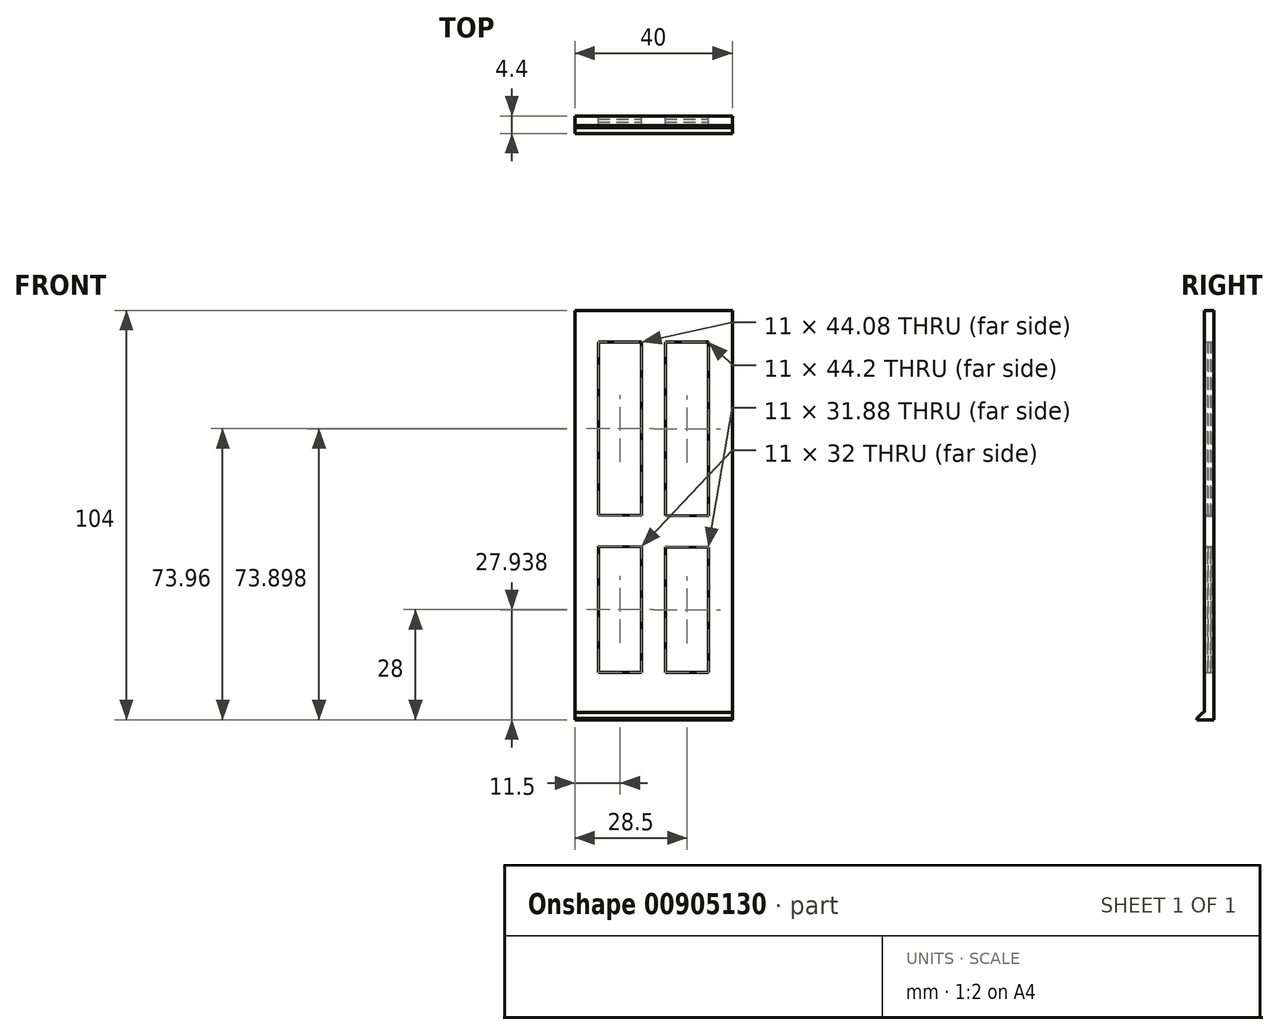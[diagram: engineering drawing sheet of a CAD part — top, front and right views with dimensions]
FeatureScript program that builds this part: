
annotation { "Feature Type Name" : "Feature", "Feature Type Description" : "" }
export const myFeature = defineFeature(function(context is Context, id is Id, definition is map)
    precondition{}
    {
        {
            var Q0;
            Q0=qCreatedBy(makeId("Front.planeOp"),FACE);
            var sketch = newSketch(context, id + "F0", { "sketchPlane" : qUnion([Q0])});
            skLineSegment(sketch, "E0.bottom", {"start": v(20, 52) * mm, "end": v(-20, 52) * mm});
            skLineSegment(sketch, "E0.top", {"start": v(20, -52) * mm, "end": v(-20, -52) * mm});
            skLineSegment(sketch, "E0.left", {"start": v(20, 52) * mm, "end": v(20, -52) * mm});
            skLineSegment(sketch, "E0.right", {"start": v(-20, 52) * mm, "end": v(-20, -52) * mm});
            skPoint(sketch, "E0.middle", {"position": v(0, 0) * mm});
            skLineSegment(sketch, "E1.0", {"start": v(-14, 52) * mm, "end": v(-14, -52) * mm});
            skLineSegment(sketch, "E2.0", {"start": v(14, 52) * mm, "end": v(14, -52.4) * mm});
            skLineSegment(sketch, "E3.0", {"start": v(20, 44) * mm, "end": v(-20, 44) * mm});
            skLineSegment(sketch, "E4.0", {"start": v(20, -40) * mm, "end": v(-20, -40) * mm});
            skLineSegment(sketch, "E5", {"start": v(0, -40) * mm, "end": v(0, 44) * mm, "construction": true});
            skLineSegment(sketch, "E6.0", {"start": v(3, -40) * mm, "end": v(3, 44) * mm});
            skLineSegment(sketch, "E7.0", {"start": v(-3, -40) * mm, "end": v(-3, 44) * mm});
            skLineSegment(sketch, "E8", {"start": v(-14, 0) * mm, "end": v(14, -0.2) * mm, "construction": true});
            skLineSegment(sketch, "E9", {"start": v(-14, 0) * mm, "end": v(14, -0.2) * mm});
            skLineSegment(sketch, "E10.0", {"start": v(-14, -8) * mm, "end": v(14, -8.2) * mm});
            skSolve(sketch);
        }
        {
            var Q0;
            {var subQ0=sQuery(id+"F0.wireOp",EDGE,"E9");var subQ1=sQuery(id+"F0.wireOp",EDGE,"E1.0");var subQ2=makeQuery(id+"F0.imprint","INTERSECT",VERTEX,{"derivedFrom":[subQ1,subQ0]});Q0=makeQuery(id+"F0.imprint","IMPRINT",FACE,{"disambiguationData":[TD([[makeQuery(id+"F0.imprint","IMPRINT",EDGE,{"disambiguationData":[TD([[subQ2,1.0]])],"derivedFrom":subQ1}),1.0]])]});}
            var Q1;
            {var subQ0=sQuery(id+"F0.wireOp",EDGE,"E9");var subQ1=sQuery(id+"F0.wireOp",EDGE,"E2.0");var subQ2=makeQuery(id+"F0.imprint","INTERSECT",VERTEX,{"derivedFrom":[subQ1,subQ0]});Q1=makeQuery(id+"F0.imprint","IMPRINT",FACE,{"disambiguationData":[TD([[makeQuery(id+"F0.imprint","IMPRINT",EDGE,{"disambiguationData":[TD([[subQ2,1.0]])],"derivedFrom":subQ1}),-1.0]])]});}
            var Q2;
            {var subQ0=sQuery(id+"F0.wireOp",EDGE,"E10.0");var subQ1=sQuery(id+"F0.wireOp",EDGE,"E1.0");var subQ2=makeQuery(id+"F0.imprint","INTERSECT",VERTEX,{"derivedFrom":[subQ1,subQ0]});Q2=makeQuery(id+"F0.imprint","IMPRINT",FACE,{"disambiguationData":[TD([[makeQuery(id+"F0.imprint","IMPRINT",EDGE,{"disambiguationData":[TD([[subQ2,-1.0]])],"derivedFrom":subQ1}),1.0]])]});}
            var Q3;
            {var subQ0=sQuery(id+"F0.wireOp",EDGE,"E10.0");var subQ1=sQuery(id+"F0.wireOp",EDGE,"E2.0");var subQ2=makeQuery(id+"F0.imprint","INTERSECT",VERTEX,{"derivedFrom":[subQ1,subQ0]});Q3=makeQuery(id+"F0.imprint","IMPRINT",FACE,{"disambiguationData":[TD([[makeQuery(id+"F0.imprint","IMPRINT",EDGE,{"disambiguationData":[TD([[subQ2,-1.0]])],"derivedFrom":subQ1}),-1.0]])]});}
            extrude(context, id + "F1", {"entities" : qUnion([Q0, Q1, Q2, Q3]), "depth" : .4 * mm, "offsetDistance" : 25 * mm, "hasSecondDirection" : true, "secondDirectionOppositeDirection" : true, "secondDirectionDepth" : .4 * mm});
        }
        {
            var Q0;
            {var subQ0=sQuery(id+"F0.wireOp",EDGE,"E0.right");var subQ1=sQuery(id+"F0.wireOp",EDGE,"E0.bottom");var subQ2=makeQuery(id+"F0.imprint","INTERSECT",VERTEX,{"derivedFrom":[subQ1,subQ0]});Q0=makeQuery(id+"F0.imprint","IMPRINT",FACE,{"disambiguationData":[TD([[makeQuery(id+"F0.imprint","IMPRINT",EDGE,{"disambiguationData":[TD([[subQ2,1.0]])],"derivedFrom":subQ1}),1.0]])]});}
            var Q1;
            {var subQ4=sQuery(id+"F0.wireOp",EDGE,"E1.0");var subQ5=sQuery(id+"F0.wireOp",EDGE,"E0.bottom");var subQ6=makeQuery(id+"F0.imprint","INTERSECT",VERTEX,{"derivedFrom":[subQ5,subQ4]});Q1=makeQuery(id+"F0.imprint","IMPRINT",FACE,{"disambiguationData":[TD([[makeQuery(id+"F0.imprint","IMPRINT",EDGE,{"disambiguationData":[TD([[subQ6,1.0]])],"derivedFrom":subQ5}),1.0]])]});}
            var Q2;
            {var subQ0=sQuery(id+"F0.wireOp",EDGE,"E0.left");var subQ1=sQuery(id+"F0.wireOp",EDGE,"E0.bottom");var subQ2=makeQuery(id+"F0.imprint","INTERSECT",VERTEX,{"derivedFrom":[subQ1,subQ0]});Q2=makeQuery(id+"F0.imprint","IMPRINT",FACE,{"disambiguationData":[TD([[makeQuery(id+"F0.imprint","IMPRINT",EDGE,{"disambiguationData":[TD([[subQ2,-1.0]])],"derivedFrom":subQ1}),1.0]])]});}
            var Q3;
            {var subQ5=sQuery(id+"F0.wireOp",EDGE,"E3.0");var subQ7=sQuery(id+"F0.wireOp",EDGE,"E0.left");var subQ8=makeQuery(id+"F0.imprint","INTERSECT",VERTEX,{"derivedFrom":[subQ7,subQ5]});Q3=makeQuery(id+"F0.imprint","IMPRINT",FACE,{"disambiguationData":[TD([[makeQuery(id+"F0.imprint","IMPRINT",EDGE,{"disambiguationData":[TD([[subQ8,-1.0]])],"derivedFrom":subQ7}),-1.0]])]});}
            var Q4;
            {var subQ0=sQuery(id+"F0.wireOp",EDGE,"E6.0");var subQ1=sQuery(id+"F0.wireOp",EDGE,"E3.0");var subQ2=makeQuery(id+"F0.imprint","INTERSECT",VERTEX,{"derivedFrom":[subQ1,subQ0]});Q4=makeQuery(id+"F0.imprint","IMPRINT",FACE,{"disambiguationData":[TD([[makeQuery(id+"F0.imprint","IMPRINT",EDGE,{"disambiguationData":[TD([[subQ2,-1.0]])],"derivedFrom":subQ1}),1.0]])]});}
            var Q5;
            {var subQ3=sQuery(id+"F0.wireOp",EDGE,"E3.0");var subQ7=sQuery(id+"F0.wireOp",EDGE,"E0.right");var subQ8=makeQuery(id+"F0.imprint","INTERSECT",VERTEX,{"derivedFrom":[subQ7,subQ3]});Q5=makeQuery(id+"F0.imprint","IMPRINT",FACE,{"disambiguationData":[TD([[makeQuery(id+"F0.imprint","IMPRINT",EDGE,{"disambiguationData":[TD([[subQ8,-1.0]])],"derivedFrom":subQ7}),1.0]])]});}
            var Q6;
            {var subQ0=sQuery(id+"F0.wireOp",EDGE,"E9");var subQ1=sQuery(id+"F0.wireOp",EDGE,"E1.0");var subQ2=makeQuery(id+"F0.imprint","INTERSECT",VERTEX,{"derivedFrom":[subQ1,subQ0]});Q6=makeQuery(id+"F0.imprint","IMPRINT",FACE,{"disambiguationData":[TD([[makeQuery(id+"F0.imprint","IMPRINT",EDGE,{"disambiguationData":[TD([[subQ2,-1.0]])],"derivedFrom":subQ1}),1.0]])]});}
            var Q7;
            {var subQ0=sQuery(id+"F0.wireOp",EDGE,"E10.0");var subQ1=sQuery(id+"F0.wireOp",EDGE,"E6.0");var subQ2=makeQuery(id+"F0.imprint","INTERSECT",VERTEX,{"derivedFrom":[subQ1,subQ0]});Q7=makeQuery(id+"F0.imprint","IMPRINT",FACE,{"disambiguationData":[TD([[makeQuery(id+"F0.imprint","IMPRINT",EDGE,{"disambiguationData":[TD([[subQ2,-1.0]])],"derivedFrom":subQ1}),1.0]])]});}
            var Q8;
            {var subQ0=sQuery(id+"F0.wireOp",EDGE,"E9");var subQ1=sQuery(id+"F0.wireOp",EDGE,"E2.0");var subQ2=makeQuery(id+"F0.imprint","INTERSECT",VERTEX,{"derivedFrom":[subQ1,subQ0]});Q8=makeQuery(id+"F0.imprint","IMPRINT",FACE,{"disambiguationData":[TD([[makeQuery(id+"F0.imprint","IMPRINT",EDGE,{"disambiguationData":[TD([[subQ2,-1.0]])],"derivedFrom":subQ1}),-1.0]])]});}
            var Q9;
            {var subQ0=sQuery(id+"F0.wireOp",EDGE,"E6.0");var subQ1=sQuery(id+"F0.wireOp",EDGE,"E4.0");var subQ2=makeQuery(id+"F0.imprint","INTERSECT",VERTEX,{"derivedFrom":[subQ1,subQ0]});Q9=makeQuery(id+"F0.imprint","IMPRINT",FACE,{"disambiguationData":[TD([[makeQuery(id+"F0.imprint","IMPRINT",EDGE,{"disambiguationData":[TD([[subQ2,-1.0]])],"derivedFrom":subQ1}),-1.0]])]});}
            var Q10;
            {var subQ0=sQuery(id+"F0.wireOp",EDGE,"E0.right");var subQ1=sQuery(id+"F0.wireOp",EDGE,"E0.top");var subQ2=makeQuery(id+"F0.imprint","INTERSECT",VERTEX,{"derivedFrom":[subQ1,subQ0]});Q10=makeQuery(id+"F0.imprint","IMPRINT",FACE,{"disambiguationData":[TD([[makeQuery(id+"F0.imprint","IMPRINT",EDGE,{"disambiguationData":[TD([[subQ2,1.0]])],"derivedFrom":subQ1}),-1.0]])]});}
            var Q11;
            {var subQ4=sQuery(id+"F0.wireOp",EDGE,"E0.top");var subQ6=sQuery(id+"F0.wireOp",EDGE,"E1.0");var subQ7=makeQuery(id+"F0.imprint","INTERSECT",VERTEX,{"derivedFrom":[subQ4,subQ6]});Q11=makeQuery(id+"F0.imprint","IMPRINT",FACE,{"disambiguationData":[TD([[makeQuery(id+"F0.imprint","IMPRINT",EDGE,{"disambiguationData":[TD([[subQ7,1.0]])],"derivedFrom":subQ4}),-1.0]])]});}
            var Q12;
            {var subQ0=sQuery(id+"F0.wireOp",EDGE,"E0.left");var subQ1=sQuery(id+"F0.wireOp",EDGE,"E0.top");var subQ2=makeQuery(id+"F0.imprint","INTERSECT",VERTEX,{"derivedFrom":[subQ1,subQ0]});Q12=makeQuery(id+"F0.imprint","IMPRINT",FACE,{"disambiguationData":[TD([[makeQuery(id+"F0.imprint","IMPRINT",EDGE,{"disambiguationData":[TD([[subQ2,-1.0]])],"derivedFrom":subQ1}),-1.0]])]});}
            extrude(context, id + "F2", {"entities" : qUnion([Q0, Q1, Q2, Q3, Q4, Q5, Q6, Q7, Q8, Q9, Q10, Q11, Q12]), "depth" : 1.2 * mm, "offsetDistance" : 25 * mm, "hasSecondDirection" : true, "secondDirectionOppositeDirection" : true, "secondDirectionDepth" : 1.2 * mm});
        }
        {
            var Q0;
            Q0=makeQuery(id+"F2.opExtrude","CAP_FACE",FACE,{"disambiguationData":[OSD([sQuery(id+"F0.wireOp",EDGE,"E0.bottom"),sQuery(id+"F0.wireOp",EDGE,"E0.top"),sQuery(id+"F0.wireOp",EDGE,"E0.left"),sQuery(id+"F0.wireOp",EDGE,"E0.right"),sQuery(id+"F0.wireOp",EDGE,"E1.0"),sQuery(id+"F0.wireOp",EDGE,"E2.0"),sQuery(id+"F0.wireOp",EDGE,"E3.0"),sQuery(id+"F0.wireOp",EDGE,"E4.0"),sQuery(id+"F0.wireOp",EDGE,"E6.0"),sQuery(id+"F0.wireOp",EDGE,"E7.0"),sQuery(id+"F0.wireOp",EDGE,"E9"),sQuery(id+"F0.wireOp",EDGE,"E10.0")])],"isStart":false});
            var sketch = newSketch(context, id + "F3", { "sketchPlane" : qUnion([Q0])});
            skLineSegment(sketch, "E11.bottom", {"start": v(-20, -52) * mm, "end": v(20, -52) * mm});
            skLineSegment(sketch, "E11.top", {"start": v(-20, -50.2) * mm, "end": v(20, -50.2) * mm});
            skLineSegment(sketch, "E11.left", {"start": v(-20, -52) * mm, "end": v(-20, -50.2) * mm});
            skLineSegment(sketch, "E11.right", {"start": v(20, -52) * mm, "end": v(20, -50.2) * mm});
            skSolve(sketch);
        }
        {
            var Q0;
            Q0=makeQuery(id+"F3.imprint","IMPRINT",FACE,{"disambiguationData":[TD([[makeQuery(id+"F3.imprint","IMPRINT",EDGE,{"derivedFrom":sQuery(id+"F3.wireOp",EDGE,"E11.bottom")}),-1.0]])]});
            extrude(context, id + "F4", {"entities" : qUnion([Q0]), "operationType" : NewBodyOperationType.ADD, "depth" : 2 * mm, "offsetDistance" : 25 * mm});
        }
        {
            var Q0;
            Q0=makeQuery(id+"F4.opExtrude","CAP_EDGE",EDGE,{"disambiguationData":[OSD([sQuery(id+"F3.wireOp",EDGE,"E11.top")])],"isStart":false});
            chamfer(context, id + "F5", {"entities" : qUnion([Q0]), "width" : 1.5 * mm, "tangentPropagation" : true});
        }
    });
